# Revit family: Green Dot Sign® ADA
name_source: partatom
category: Generic Models
units: mm (PartAtom-declared; Revit-internal decimal feet)

## family parameters
Always vertical = Yes
Can host rebar = No
Cut with Voids When Loaded = No
Host = Wall
Part Type = Normal
Room Calculation Point = No
Round Connector Dimension = Use Diameter
Shared = No

## types (28) — shared parameters
Text Height = 0' - 0 5/8"
Text Spacing = 0' - 0 3/8"
URL = https://www.greendotsign.com

## per-type parameters (varying)
| type | Band Color | Base Finish | Braille Finish | Chamfered Edge | Color Band | Color Band Edge Inset | Eased Edge | Height | Text Finish | Thickness | Width |
| Aluminum 7.25 x 9.25 | <By Category> | Green Dot Sign® Red | Green Dot Sign® Red | No | No | 0' - 0" | Yes | 0' - 7 1/4" | Green Dot Sign® Aluminum | 0' - 0 3/16" | 0' - 9 1/4" |
| Birch Plywood 7.25 x 9.25 | <By Category> | Green Dot Sign® Birch Plywood | Green Dot Sign® Brown | No | No | 0' - 0" | Yes | 0' - 7 1/4" | Green Dot Sign® Brown | 0' - 0 1/4" | 0' - 9 1/4" |
| Aspen Eased Color Band 9.25 x 9.25 | Green Dot Sign® Kelly Green | Green Dot Sign® Aspen | Green Dot Sign® Black | No | Yes | 0' - 0" | Yes | 0' - 9 1/4" | Green Dot Sign® Black | 0' - 0 11/16" | 0' - 9 1/4" |
| Aspen Chamfered 9.25 x 9.25 | <By Category> | Green Dot Sign® Aspen | Green Dot Sign® Blue | Yes | No | 0' - 0 5/32" | No | 0' - 9 1/4" | Green Dot Sign® Blue | 0' - 0 11/16" | 0' - 9 1/4" |
| Aspen Chamfered 7.25 x 9.25 | <By Category> | Green Dot Sign® Aspen | Green Dot Sign® Light Blue | Yes | No | 0' - 0 5/32" | No | 0' - 7 1/4" | Green Dot Sign® Light Blue | 0' - 0 11/16" | 0' - 9 1/4" |
| Aspen Eased Color Band 7.25 x 9.25 | Green Dot Sign® Orange | Green Dot Sign® Aspen | Green Dot Sign® Black | No | Yes | 0' - 0" | Yes | 0' - 7 1/4" | Green Dot Sign® Black | 0' - 0 11/16" | 0' - 9 1/4" |
| Aspen Eased 9.25 x 11.25 | <By Category> | Green Dot Sign® Aspen | Green Dot Sign® Forest Green | No | No | 0' - 0" | Yes | 0' - 9 1/4" | Green Dot Sign® Forest Green | 0' - 0 11/16" | 0' - 11 1/4" |
| Aspen Eased 9.25 x 9.25 | <By Category> | Green Dot Sign® Aspen | Green Dot Sign® Kelly Green | No | No | 0' - 0" | Yes | 0' - 9 1/4" | Green Dot Sign® Kelly Green | 0' - 0 11/16" | 0' - 9 1/4" |
| Aspen Eased 7.25 x 9.25 | <By Category> | Green Dot Sign® Aspen | Green Dot Sign® Orange | No | No | 0' - 0" | Yes | 0' - 7 1/4" | Green Dot Sign® Orange | 0' - 0 11/16" | 0' - 9 1/4" |
| Birch Plywood Color Band 7.25 x 9.25 | Green Dot Sign® Brown | Green Dot Sign® Birch Plywood | Green Dot Sign® Black | No | Yes | 0' - 0" | Yes | 0' - 7 1/4" | Green Dot Sign® Black | 0' - 0 1/4" | 0' - 9 1/4" |
| Aspen Chamfered Color Band 7.25 x 9.25 | Green Dot Sign® Light Blue | Green Dot Sign® Aspen | Green Dot Sign® Black | Yes | Yes | 0' - 0 5/32" | No | 0' - 7 1/4" | Green Dot Sign® Black | 0' - 0 11/16" | 0' - 9 1/4" |
| Aluminum 9.25 x 11.25 | <By Category> | Green Dot Sign® Red | Green Dot Sign® Red | No | No | 0' - 0" | Yes | 0' - 9 1/4" | Green Dot Sign® Bronze | 0' - 0 3/16" | 0' - 11 1/4" |
| Aluminum 9.25 x 9.25 | <By Category> | Green Dot Sign® Black | Green Dot Sign® Black | No | No | 0' - 0" | Yes | 0' - 9 1/4" | Green Dot Sign® Bronze | 0' - 0 3/16" | 0' - 9 1/4" |
| Birch Plywood 9.25 x 11.25 | <By Category> | Green Dot Sign® Birch Plywood | Green Dot Sign® Dark Grey | No | No | 0' - 0" | Yes | 0' - 9 1/4" | Green Dot Sign® Dark Grey | 0' - 0 1/4" | 0' - 11 1/4" |
| Birch Plywood 9.25 x 9.25 | <By Category> | Green Dot Sign® Birch Plywood | Green Dot Sign® Grey | No | No | 0' - 0" | Yes | 0' - 9 1/4" | Green Dot Sign® Grey | 0' - 0 1/4" | 0' - 9 1/4" |
| Birch Plywood Color Band 9.25 x 11.25 | Green Dot Sign® Dark Grey | Green Dot Sign® Birch Plywood | Green Dot Sign® White | No | Yes | 0' - 0" | Yes | 0' - 9 1/4" | Green Dot Sign® White | 0' - 0 1/4" | 0' - 11 1/4" |
| Birch Plywood Color Band 9.25 x 9.25 | Green Dot Sign® Grey | Green Dot Sign® Birch Plywood | Green Dot Sign® Black | No | Yes | 0' - 0" | Yes | 0' - 9 1/4" | Green Dot Sign® Black | 0' - 0 1/4" | 0' - 9 1/4" |
| Aspen Eased Color Band 9.25 x 11.25 | Green Dot Sign® Forest Green | Green Dot Sign® Aspen | Green Dot Sign® Black | No | Yes | 0' - 0" | Yes | 0' - 9 1/4" | Green Dot Sign® Black | 0' - 0 11/16" | 0' - 11 1/4" |
| Aspen Chamfered Color Band 9.25 x 11.25 | Green Dot Sign® Purple | Green Dot Sign® Aspen | Green Dot Sign® White | Yes | Yes | 0' - 0 5/32" | No | 0' - 9 1/4" | Green Dot Sign® White | 0' - 0 11/16" | 0' - 11 1/4" |
| Aspen Chamfered Color Band 9.25 x 9.25 | Green Dot Sign® Blue | Green Dot Sign® Aspen | Green Dot Sign® White | Yes | Yes | 0' - 0 5/32" | No | 0' - 9 1/4" | Green Dot Sign® White | 0' - 0 11/16" | 0' - 9 1/4" |
| Aspen Chamfered Color Band 4 x 7.25 | Green Dot Sign® Teal | Green Dot Sign® Aspen | Green Dot Sign® Black | Yes | Yes | 0' - 0 5/32" | No | 0' - 4" | Green Dot Sign® Black | 0' - 0 11/16" | 0' - 7 1/4" |
| Aluminum 4 x 7.25 | <By Category> | Green Dot Sign® Black | Green Dot Sign® Black | No | No | 0' - 0" | Yes | 0' - 4" | Green Dot Sign® Aluminum | 0' - 0 3/16" | 0' - 7 1/4" |
| Aspen Eased 4 x 7.25 | <By Category> | Green Dot Sign® Aspen | Green Dot Sign® Red | No | No | 0' - 0" | Yes | 0' - 4" | Green Dot Sign® Red | 0' - 0 11/16" | 0' - 7 1/4" |
| Birch Plywood Color Band 4 x 7.25 | Green Dot Sign® Hot Pink | Green Dot Sign® Aspen | Green Dot Sign® Black | No | Yes | 0' - 0" | Yes | 0' - 4" | Green Dot Sign® Black | 0' - 0 1/4" | 0' - 7 1/4" |
| Birch Plywood 4 x 7.25 | <By Category> | Green Dot Sign® Birch Plywood | Green Dot Sign® Hot Pink | No | No | 0' - 0" | Yes | 0' - 4" | Green Dot Sign® Hot Pink | 0' - 0 1/4" | 0' - 7 1/4" |
| Aspen Eased Color Band 4 x 7.25 | Green Dot Sign® Red | Green Dot Sign® Aspen | Green Dot Sign® Black | No | Yes | 0' - 0" | Yes | 0' - 4" | Green Dot Sign® Black | 0' - 0 11/16" | 0' - 7 1/4" |
| Aspen Chamfered 4 x 7.25 | <By Category> | Green Dot Sign® Aspen | Green Dot Sign® Teal | Yes | No | 0' - 0 5/32" | No | 0' - 4" | Green Dot Sign® Teal | 0' - 0 11/16" | 0' - 7 1/4" |
| Aspen Chamfered 9.25 x 11.25 | <By Category> | Green Dot Sign® Aspen | Green Dot Sign® Purple | Yes | No | 0' - 0 5/32" | No | 0' - 9 1/4" | Green Dot Sign® Purple | 0' - 0 11/16" | 0' - 11 1/4" |

## geometry (parser evidence)
native form markers: Sweep x10
no freeform markers — native parametric forms only
